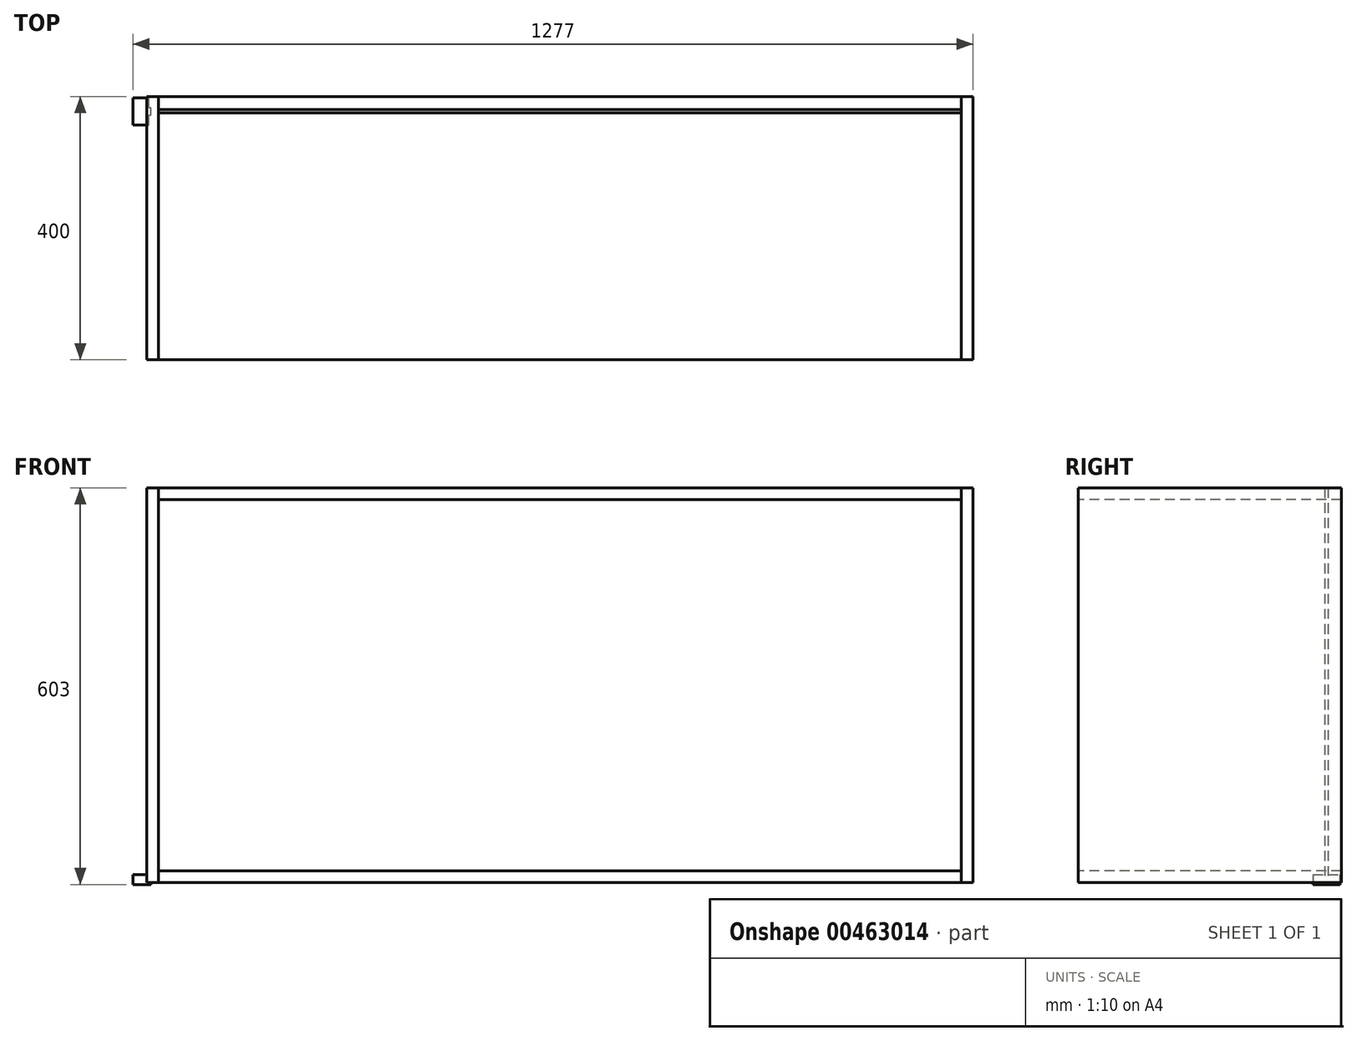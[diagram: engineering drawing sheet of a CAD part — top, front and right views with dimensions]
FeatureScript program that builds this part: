
annotation { "Feature Type Name" : "Feature", "Feature Type Description" : "" }
export const myFeature = defineFeature(function(context is Context, id is Id, definition is map)
    precondition{}
    {
        {
            assignVariable(context, id + "F0", {"name" : "storageWidth", "anyValue" : 1256});
        }
        {
            assignVariable(context, id + "F1", {"name" : "plyWidth", "anyValue" : 18});
        }
        {
            var Q0;
            Q0=qCreatedBy(makeId("Front.planeOp"),FACE);
            var sketch = newSketch(context, id + "F2", { "sketchPlane" : qUnion([Q0])});
            skLineSegment(sketch, "E0.top", {"start": v(0, 0) * mm, "end": v(1238, 0) * mm, "construction": true});
            skLineSegment(sketch, "E0.left", {"start": v(0, 600) * mm, "end": v(0, 0) * mm, "construction": true});
            skLineSegment(sketch, "E0.right", {"start": v(1238, 600) * mm, "end": v(1238, 0) * mm});
            skLineSegment(sketch, "E1", {"start": v(18, 600) * mm, "end": v(18, 0) * mm});
            skLineSegment(sketch, "E2", {"start": v(0, 600) * mm, "end": v(18, 600) * mm, "construction": true});
            skLineSegment(sketch, "E3", {"start": v(18, 600) * mm, "end": v(1238, 600) * mm});
            skLineSegment(sketch, "E4", {"start": v(18, 0) * mm, "end": v(1238, 0) * mm});
            skLineSegment(sketch, "E5", {"start": v(1256, 600) * mm, "end": v(1256, 0) * mm, "construction": true});
            skLineSegment(sketch, "E6", {"start": v(0, 300) * mm, "end": v(1256, 300) * mm, "construction": true});
            skSolve(sketch);
        }
        {
            var Q0;
            Q0 = qSketchRegion(id + "F2", true);
            var Q1;
            Q1=makeQuery(id+"F2.imprint","IMPRINT",FACE,{"disambiguationData":[TD([[makeQuery(id+"F2.imprint","IMPRINT",EDGE,{"derivedFrom":sQuery(id+"F2.wireOp",EDGE,"E0.bottom")}),-1.0]])]});
            extrude(context, id + "F3", {"entities" : qUnion([Q0, Q1]), "depth" : 5 * mm});
        }
        {
            var Q0;
            Q0=qCreatedBy(makeId("Right.planeOp"),FACE);
            var sketch = newSketch(context, id + "F4", { "sketchPlane" : qUnion([Q0])});
            skLineSegment(sketch, "E7.bottom", {"start": v(20, 0) * mm, "end": v(-380, 0) * mm});
            skLineSegment(sketch, "E7.top", {"start": v(20, 600) * mm, "end": v(-380, 600) * mm});
            skLineSegment(sketch, "E7.left", {"start": v(20, 0) * mm, "end": v(20, 600) * mm});
            skLineSegment(sketch, "E7.right", {"start": v(-380, 0) * mm, "end": v(-380, 600) * mm});
            skLineSegment(sketch, "E8", {"start": v(20, 0) * mm, "end": v(0, 0) * mm});
            skSolve(sketch);
        }
        {
            var Q0;
            Q0=makeQuery(id+"F4.imprint","IMPRINT",FACE,{"disambiguationData":[TD([[makeQuery(id+"F4.imprint","IMPRINT",EDGE,{"derivedFrom":sQuery(id+"F4.wireOp",EDGE,"E7.bottom")}),-1.0]])]});
            extrude(context, id + "F5", {"entities" : qUnion([Q0]), "depth" : getVariable(context, 'plyWidth') * mm});
        }
        {
            var Q0;
            Q0=makeQuery(id+"F5.opExtrude","SWEPT_BODY",BODY,{"disambiguationData":[OSD([sQuery(id+"F4.wireOp",EDGE,"E7.bottom"),sQuery(id+"F4.wireOp",EDGE,"E7.top"),sQuery(id+"F4.wireOp",EDGE,"E7.left"),sQuery(id+"F4.wireOp",EDGE,"E7.right"),sQuery(id+"F4.wireOp",EDGE,"E8")])]});
            transform(context, id + "F6", {"entities" : qUnion([Q0]), "transformType" : TransformType.TRANSLATION_3D, "dx" : (getVariable(context, 'storageWidth') - getVariable(context, 'plyWidth')) * mm, "dy" : 0 * mm, "dz" : 0 * mm, "makeCopy" : true});
        }
        {
            var Q0;
            Q0=qCreatedBy(makeId("Top.planeOp"),FACE);
            var sketch = newSketch(context, id + "F7", { "sketchPlane" : qUnion([Q0])});
            skLineSegment(sketch, "E9", {"start": v(0, 0) * mm, "end": v(0, 15) * mm});
            skLineSegment(sketch, "E10", {"start": v(0, 15) * mm, "end": v(-18, 15) * mm});
            skLineSegment(sketch, "E11", {"start": v(-18, 15) * mm, "end": v(-18, -20) * mm});
            skLineSegment(sketch, "E12", {"start": v(-18, -20) * mm, "end": v(0, -20) * mm});
            skLineSegment(sketch, "E13", {"start": v(0, -20) * mm, "end": v(0, -5) * mm});
            skLineSegment(sketch, "E14", {"start": v(0, -5) * mm, "end": v(3.6, -5) * mm});
            skLineSegment(sketch, "E15", {"start": v(3.6, -5) * mm, "end": v(3.6, 0) * mm});
            skLineSegment(sketch, "E16", {"start": v(3.6, 0) * mm, "end": v(0, 0) * mm});
            skLineSegment(sketch, "E17.0", {"start": v(3, 3) * mm, "end": v(3, 18) * mm});
            skLineSegment(sketch, "E17.1", {"start": v(6.6, 3) * mm, "end": v(3, 3) * mm});
            skLineSegment(sketch, "E17.2", {"start": v(3, 18) * mm, "end": v(-21, 18) * mm});
            skLineSegment(sketch, "E17.3", {"start": v(6.6, -8) * mm, "end": v(6.6, 3) * mm});
            skLineSegment(sketch, "E17.4", {"start": v(-21, 18) * mm, "end": v(-21, -23) * mm});
            skLineSegment(sketch, "E17.5", {"start": v(-21, -23) * mm, "end": v(3, -23) * mm});
            skLineSegment(sketch, "E17.6", {"start": v(3, -23) * mm, "end": v(3, -8) * mm});
            skLineSegment(sketch, "E17.7", {"start": v(3, -8) * mm, "end": v(6.6, -8) * mm});
            skSolve(sketch);
        }
        {
            var Q0;
            Q0=makeQuery(id+"F7.imprint","IMPRINT",FACE,{"disambiguationData":[TD([[makeQuery(id+"F7.imprint","IMPRINT",EDGE,{"derivedFrom":sQuery(id+"F7.wireOp",EDGE,"E9")}),1.0]])]});
            var Q1;
            Q1=makeQuery(id+"F7.imprint","IMPRINT",FACE,{"disambiguationData":[TD([[makeQuery(id+"F7.imprint","IMPRINT",EDGE,{"derivedFrom":sQuery(id+"F7.wireOp",EDGE,"E9")}),-1.0]])]});
            extrude(context, id + "F8", {"entities" : qUnion([Q0, Q1]), "depth" : 12 * mm, "hasSecondDirection" : true, "secondDirectionOppositeDirection" : true, "secondDirectionDepth" : 3 * mm});
        }
        {
            var Q0;
            Q0=makeQuery(id+"F3.opExtrude","SWEPT_BODY",BODY,{"disambiguationData":[OSD([sQuery(id+"F2.wireOp",EDGE,"E0.bottom"),sQuery(id+"F2.wireOp",EDGE,"E0.top"),sQuery(id+"F2.wireOp",EDGE,"E0.left"),sQuery(id+"F2.wireOp",EDGE,"E0.right")])]});
            var Q1;
            Q1=makeQuery(id+"F5.opExtrude","SWEPT_BODY",BODY,{"disambiguationData":[OSD([sQuery(id+"F4.wireOp",EDGE,"E7.bottom"),sQuery(id+"F4.wireOp",EDGE,"E7.top"),sQuery(id+"F4.wireOp",EDGE,"E7.left"),sQuery(id+"F4.wireOp",EDGE,"E7.right"),sQuery(id+"F4.wireOp",EDGE,"E8")])]});
            var Q2;
            Q2=makeQuery(id+"F6.opPattern","COPY",BODY,{"derivedFrom":makeQuery(id+"F5.opExtrude","SWEPT_BODY",BODY,{"disambiguationData":[OSD([sQuery(id+"F4.wireOp",EDGE,"E7.bottom"),sQuery(id+"F4.wireOp",EDGE,"E7.top"),sQuery(id+"F4.wireOp",EDGE,"E7.left"),sQuery(id+"F4.wireOp",EDGE,"E7.right"),sQuery(id+"F4.wireOp",EDGE,"E8")])]}),"instanceName":"1"});
            var Q3;
            Q3=makeQuery(id+"F8.opExtrude","SWEPT_BODY",BODY,{"disambiguationData":[OSD([sQuery(id+"F7.wireOp",EDGE,"E17.0"),sQuery(id+"F7.wireOp",EDGE,"E17.1"),sQuery(id+"F7.wireOp",EDGE,"E17.2"),sQuery(id+"F7.wireOp",EDGE,"E17.3"),sQuery(id+"F7.wireOp",EDGE,"E17.4"),sQuery(id+"F7.wireOp",EDGE,"E17.5"),sQuery(id+"F7.wireOp",EDGE,"E17.6"),sQuery(id+"F7.wireOp",EDGE,"E17.7")])]});
            booleanBodies(context, id + "F9", {"operationType" : BooleanOperationType.SUBTRACTION, "tools" : qUnion([Q0, Q1, Q2]), "targets" : qUnion([Q3]), "keepTools" : true});
        }
        {
            var Q0;
            Q0=qCreatedBy(makeId("Top.planeOp"),FACE);
            var sketch = newSketch(context, id + "F10", { "sketchPlane" : qUnion([Q0])});
            skLineSegment(sketch, "E18.bottom", {"start": v(18, 20) * mm, "end": v(1238, 20) * mm});
            skLineSegment(sketch, "E18.top", {"start": v(18, -380) * mm, "end": v(1238, -380) * mm});
            skLineSegment(sketch, "E18.left", {"start": v(18, 20) * mm, "end": v(18, -380) * mm});
            skLineSegment(sketch, "E18.right", {"start": v(1238, 20) * mm, "end": v(1238, -380) * mm});
            skSolve(sketch);
        }
        {
            var Q0;
            Q0 = qSketchRegion(id + "F10", true);
            extrude(context, id + "F11", {"entities" : qUnion([Q0]), "depth" : (getVariable(context, 'plyWidth')) * mm});
        }
        {
            var Q0;
            Q0=makeQuery(id+"F11.opExtrude","SWEPT_BODY",BODY,{"disambiguationData":[OSD([sQuery(id+"F10.wireOp",EDGE,"E18.bottom"),sQuery(id+"F10.wireOp",EDGE,"E18.top"),sQuery(id+"F10.wireOp",EDGE,"E18.left"),sQuery(id+"F10.wireOp",EDGE,"E18.right")])]});
            transform(context, id + "F12", {"entities" : qUnion([Q0]), "transformType" : TransformType.TRANSLATION_3D, "dx" : 0 * mm, "dy" : 0 * mm, "dz" : (600 - getVariable(context, 'plyWidth')) * mm, "makeCopy" : true});
        }
    });
